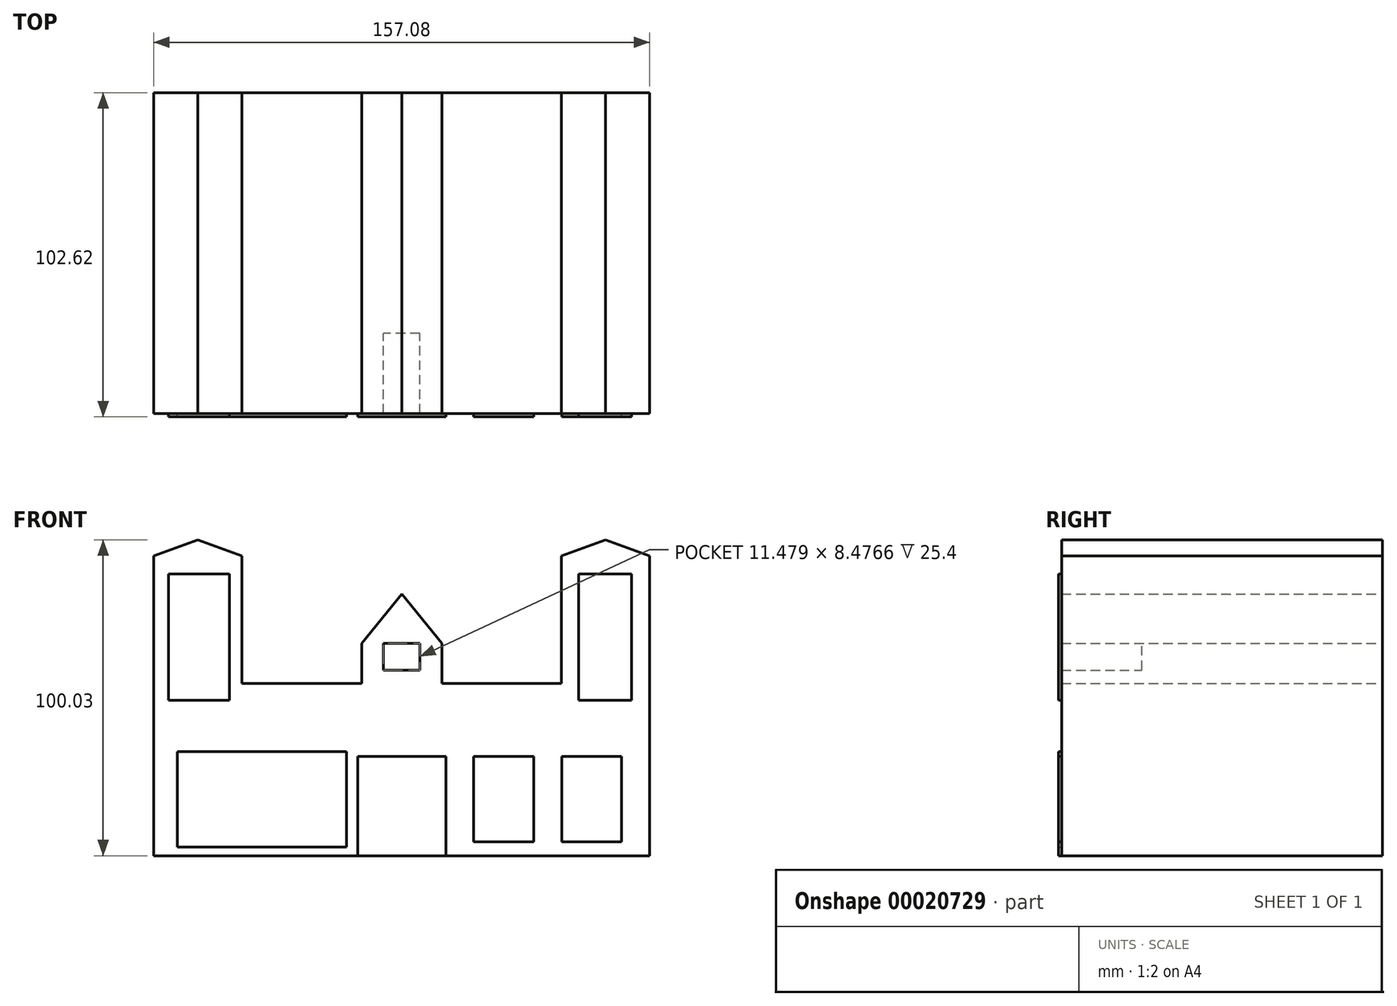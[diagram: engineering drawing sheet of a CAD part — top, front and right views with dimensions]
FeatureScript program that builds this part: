
annotation { "Feature Type Name" : "Feature", "Feature Type Description" : "" }
export const myFeature = defineFeature(function(context is Context, id is Id, definition is map)
    precondition{}
    {
        {
            var Q0;
            Q0=qCreatedBy(makeId("Front.planeOp"),FACE);
            var sketch = newSketch(context, id + "F0", { "sketchPlane" : qUnion([Q0])});
            skLineSegment(sketch, "E0", {"start": v(-78.54, -44.12) * mm, "end": v(-78.54, 50.82) * mm});
            skLineSegment(sketch, "E1", {"start": v(-78.54, 50.82) * mm, "end": v(-64.6, 55.91) * mm});
            skLineSegment(sketch, "E2", {"start": v(-64.6, 55.91) * mm, "end": v(-50.66, 50.82) * mm});
            skLineSegment(sketch, "E3", {"start": v(-50.66, 50.82) * mm, "end": v(-50.66, 10.47) * mm});
            skLineSegment(sketch, "E4", {"start": v(-50.66, 10.47) * mm, "end": v(50.66, 10.47) * mm});
            skLineSegment(sketch, "E5", {"start": v(50.66, 10.47) * mm, "end": v(50.66, 50.82) * mm});
            skLineSegment(sketch, "E6", {"start": v(50.66, 50.82) * mm, "end": v(64.6, 55.91) * mm});
            skLineSegment(sketch, "E7", {"start": v(64.6, 55.91) * mm, "end": v(78.54, 50.82) * mm});
            skLineSegment(sketch, "E8", {"start": v(78.54, 50.82) * mm, "end": v(78.54, -44.12) * mm});
            skLineSegment(sketch, "E9", {"start": v(78.54, -44.12) * mm, "end": v(-78.54, -44.12) * mm});
            skLineSegment(sketch, "E10", {"start": v(-13.97, -44.12) * mm, "end": v(-13.97, -12.68) * mm});
            skLineSegment(sketch, "E11", {"start": v(-13.97, -12.68) * mm, "end": v(13.97, -12.68) * mm});
            skLineSegment(sketch, "E12", {"start": v(13.97, -12.68) * mm, "end": v(13.97, -44.12) * mm});
            skLineSegment(sketch, "E13", {"start": v(13.97, -44.12) * mm, "end": v(0, -44.12) * mm});
            skLineSegment(sketch, "E14", {"start": v(0, -44.12) * mm, "end": v(0, -12.68) * mm});
            skLineSegment(sketch, "E15", {"start": v(-12.7, 10.47) * mm, "end": v(-12.7, 23.17) * mm});
            skLineSegment(sketch, "E16", {"start": v(-12.7, 23.17) * mm, "end": v(0, 38.8) * mm});
            skLineSegment(sketch, "E17", {"start": v(0, 38.8) * mm, "end": v(12.7, 23.17) * mm});
            skLineSegment(sketch, "E18", {"start": v(12.7, 23.17) * mm, "end": v(12.7, 10.47) * mm});
            skLineSegment(sketch, "E19", {"start": v(-5.74, 23.17) * mm, "end": v(-5.74, 14.7) * mm});
            skLineSegment(sketch, "E20", {"start": v(-5.74, 14.7) * mm, "end": v(5.74, 14.7) * mm});
            skLineSegment(sketch, "E21", {"start": v(5.74, 14.7) * mm, "end": v(5.74, 23.17) * mm});
            skLineSegment(sketch, "E22", {"start": v(5.74, 23.17) * mm, "end": v(-5.74, 23.17) * mm});
            skLineSegment(sketch, "E23", {"start": v(-5.74, 23.17) * mm, "end": v(-6.35, 30.99) * mm});
            skLineSegment(sketch, "E24", {"start": v(5.74, 23.17) * mm, "end": v(6.35, 30.99) * mm});
            skLineSegment(sketch, "E25", {"start": v(-78.54, -44.12) * mm, "end": v(-13.97, -44.12) * mm});
            skLineSegment(sketch, "E26", {"start": v(-13.97, -44.12) * mm, "end": v(13.97, -44.12) * mm});
            skLineSegment(sketch, "E27", {"start": v(13.97, -44.12) * mm, "end": v(78.54, -44.12) * mm});
            skLineSegment(sketch, "E28", {"start": v(-13.97, -44.12) * mm, "end": v(0, -44.12) * mm});
            skLineSegment(sketch, "E29", {"start": v(0, -44.12) * mm, "end": v(13.97, -44.12) * mm});
            skLineSegment(sketch, "E30", {"start": v(-50.66, 10.47) * mm, "end": v(-12.7, 10.47) * mm});
            skLineSegment(sketch, "E31", {"start": v(12.7, 10.47) * mm, "end": v(50.66, 10.47) * mm});
            skLineSegment(sketch, "E32", {"start": v(-12.7, 23.17) * mm, "end": v(12.7, 23.17) * mm});
            skSolve(sketch);
        }
        {
            var Q0;
            Q0=makeQuery(id+"F0.imprint","IMPRINT",FACE,{"disambiguationData":[TD([[makeQuery(id+"F0.imprint","IMPRINT",EDGE,{"derivedFrom":sQuery(id+"F0.wireOp",EDGE,"E0")}),-1.0]])]});
            var Q1;
            Q1=makeQuery(id+"F0.imprint","IMPRINT",FACE,{"disambiguationData":[TD([[makeQuery(id+"F0.imprint","IMPRINT",EDGE,{"derivedFrom":sQuery(id+"F0.wireOp",EDGE,"E4")}),1.0]])]});
            var Q2;
            {var subQ1=sQuery(id+"F0.wireOp",EDGE,"E23");Q2=makeQuery(id+"F0.imprint","IMPRINT",FACE,{"disambiguationData":[TD([[makeQuery(id+"F0.imprint","IMPRINT",EDGE,{"derivedFrom":subQ1}),1.0]])]});}
            var Q3;
            {var subQ2=sQuery(id+"F0.wireOp",EDGE,"E23");Q3=makeQuery(id+"F0.imprint","IMPRINT",FACE,{"disambiguationData":[TD([[makeQuery(id+"F0.imprint","IMPRINT",EDGE,{"derivedFrom":subQ2}),-1.0]])]});}
            var Q4;
            {var subQ1=sQuery(id+"F0.wireOp",EDGE,"E24");Q4=makeQuery(id+"F0.imprint","IMPRINT",FACE,{"disambiguationData":[TD([[makeQuery(id+"F0.imprint","IMPRINT",EDGE,{"derivedFrom":subQ1}),-1.0]])]});}
            extrude(context, id + "F1", {"entities" : qUnion([Q0, Q1, Q2, Q3, Q4]), "depth" : 101.6 * mm});
        }
        {
            var Q0;
            Q0=makeQuery(id+"F1.opExtrude","CAP_FACE",FACE,{"disambiguationData":[OSD([sQuery(id+"F0.wireOp",EDGE,"E0"),sQuery(id+"F0.wireOp",EDGE,"E1"),sQuery(id+"F0.wireOp",EDGE,"E2"),sQuery(id+"F0.wireOp",EDGE,"E3"),sQuery(id+"F0.wireOp",EDGE,"E5"),sQuery(id+"F0.wireOp",EDGE,"E6"),sQuery(id+"F0.wireOp",EDGE,"E7"),sQuery(id+"F0.wireOp",EDGE,"E8"),sQuery(id+"F0.wireOp",EDGE,"E10"),sQuery(id+"F0.wireOp",EDGE,"E11"),sQuery(id+"F0.wireOp",EDGE,"E12"),sQuery(id+"F0.wireOp",EDGE,"E15"),sQuery(id+"F0.wireOp",EDGE,"E16"),sQuery(id+"F0.wireOp",EDGE,"E17"),sQuery(id+"F0.wireOp",EDGE,"E18"),sQuery(id+"F0.wireOp",EDGE,"E19"),sQuery(id+"F0.wireOp",EDGE,"E20"),sQuery(id+"F0.wireOp",EDGE,"E21"),sQuery(id+"F0.wireOp",EDGE,"E25"),sQuery(id+"F0.wireOp",EDGE,"E27"),sQuery(id+"F0.wireOp",EDGE,"E30"),sQuery(id+"F0.wireOp",EDGE,"E31"),sQuery(id+"F0.wireOp",EDGE,"E32")])],"isStart":false});
            var sketch = newSketch(context, id + "F2", { "sketchPlane" : qUnion([Q0])});
            skLineSegment(sketch, "E33.bottom", {"start": v(-73.92, 45.08) * mm, "end": v(-54.5, 45.08) * mm});
            skLineSegment(sketch, "E33.top", {"start": v(-73.92, 5.1) * mm, "end": v(-54.5, 5.1) * mm});
            skLineSegment(sketch, "E33.left", {"start": v(-73.92, 45.08) * mm, "end": v(-73.92, 5.1) * mm});
            skLineSegment(sketch, "E33.right", {"start": v(-54.5, 45.08) * mm, "end": v(-54.5, 5.1) * mm});
            skLineSegment(sketch, "E34.bottom", {"start": v(56.09, 45.08) * mm, "end": v(72.87, 45.08) * mm});
            skLineSegment(sketch, "E34.top", {"start": v(56.09, 5.1) * mm, "end": v(72.87, 5.1) * mm});
            skLineSegment(sketch, "E34.left", {"start": v(56.09, 45.08) * mm, "end": v(56.09, 5.1) * mm});
            skLineSegment(sketch, "E34.right", {"start": v(72.87, 45.08) * mm, "end": v(72.87, 5.1) * mm});
            skLineSegment(sketch, "E35.bottom", {"start": v(-71.12, -11.2) * mm, "end": v(-17.47, -11.2) * mm});
            skLineSegment(sketch, "E35.top", {"start": v(-71.12, -41.31) * mm, "end": v(-17.47, -41.31) * mm});
            skLineSegment(sketch, "E35.left", {"start": v(-71.12, -11.2) * mm, "end": v(-71.12, -41.31) * mm});
            skLineSegment(sketch, "E35.right", {"start": v(-17.47, -11.2) * mm, "end": v(-17.47, -41.31) * mm});
            skLineSegment(sketch, "E36.top", {"start": v(22.85, -39.66) * mm, "end": v(41.81, -39.66) * mm});
            skLineSegment(sketch, "E36.left", {"start": v(22.85, -12.68) * mm, "end": v(22.85, -39.66) * mm});
            skLineSegment(sketch, "E36.right", {"start": v(41.81, -12.68) * mm, "end": v(41.81, -39.66) * mm});
            skLineSegment(sketch, "E37.top", {"start": v(50.7, -39.66) * mm, "end": v(69.66, -39.66) * mm});
            skLineSegment(sketch, "E37.left", {"start": v(50.7, -12.68) * mm, "end": v(50.7, -39.66) * mm});
            skLineSegment(sketch, "E37.right", {"start": v(69.66, -12.68) * mm, "end": v(69.66, -39.66) * mm});
            skLineSegment(sketch, "E38", {"start": v(13.97, -12.68) * mm, "end": v(22.85, -12.68) * mm});
            skLineSegment(sketch, "E39", {"start": v(22.85, -12.68) * mm, "end": v(41.81, -12.68) * mm});
            skLineSegment(sketch, "E40", {"start": v(41.81, -12.68) * mm, "end": v(50.7, -12.68) * mm});
            skLineSegment(sketch, "E41", {"start": v(50.7, -12.68) * mm, "end": v(69.66, -12.68) * mm});
            skLineSegment(sketch, "E42", {"start": v(69.66, -12.68) * mm, "end": v(78.54, -12.68) * mm});
            skSolve(sketch);
        }
        {
            var Q0;
            Q0=makeQuery(id+"F2.imprint","IMPRINT",FACE,{"disambiguationData":[TD([[makeQuery(id+"F2.imprint","IMPRINT",EDGE,{"derivedFrom":sQuery(id+"F2.wireOp",EDGE,"E33.bottom")}),-1.0]])]});
            var Q1;
            Q1=makeQuery(id+"F2.imprint","IMPRINT",FACE,{"disambiguationData":[TD([[makeQuery(id+"F2.imprint","IMPRINT",EDGE,{"derivedFrom":sQuery(id+"F2.wireOp",EDGE,"E34.bottom")}),-1.0]])]});
            var Q2;
            Q2=makeQuery(id+"F2.imprint","IMPRINT",FACE,{"disambiguationData":[TD([[makeQuery(id+"F2.imprint","IMPRINT",EDGE,{"derivedFrom":sQuery(id+"F2.wireOp",EDGE,"E37.top")}),1.0]])]});
            var Q3;
            Q3=makeQuery(id+"F2.imprint","IMPRINT",FACE,{"disambiguationData":[TD([[makeQuery(id+"F2.imprint","IMPRINT",EDGE,{"derivedFrom":sQuery(id+"F2.wireOp",EDGE,"E36.top")}),1.0]])]});
            var Q4;
            Q4=makeQuery(id+"F2.imprint","IMPRINT",FACE,{"disambiguationData":[TD([[makeQuery(id+"F2.imprint","IMPRINT",EDGE,{"derivedFrom":sQuery(id+"F2.wireOp",EDGE,"E35.bottom")}),-1.0]])]});
            extrude(context, id + "F3", {"entities" : qUnion([Q0, Q1, Q2, Q3, Q4]), "operationType" : NewBodyOperationType.ADD, "depth" : 1.02 * mm});
        }
        {
            var Q0;
            {var subQ2=sQuery(id+"F0.wireOp",EDGE,"E19");Q0=makeQuery(id+"F0.imprint","IMPRINT",FACE,{"disambiguationData":[TD([[makeQuery(id+"F0.imprint","IMPRINT",EDGE,{"derivedFrom":subQ2}),1.0]])]});}
            extrude(context, id + "F4", {"entities" : qUnion([Q0]), "operationType" : NewBodyOperationType.ADD, "depth" : 76.2 * mm});
        }
        {
            var Q0;
            {var subQ2=sQuery(id+"F0.wireOp",EDGE,"E10");Q0=makeQuery(id+"F0.imprint","IMPRINT",FACE,{"disambiguationData":[TD([[makeQuery(id+"F0.imprint","IMPRINT",EDGE,{"derivedFrom":subQ2}),-1.0]])]});}
            var Q1;
            {var subQ1=sQuery(id+"F0.wireOp",EDGE,"E12");Q1=makeQuery(id+"F0.imprint","IMPRINT",FACE,{"disambiguationData":[TD([[makeQuery(id+"F0.imprint","IMPRINT",EDGE,{"derivedFrom":subQ1}),-1.0]])]});}
            extrude(context, id + "F5", {"entities" : qUnion([Q0, Q1]), "operationType" : NewBodyOperationType.ADD, "depth" : 102.62 * mm});
        }
    });
